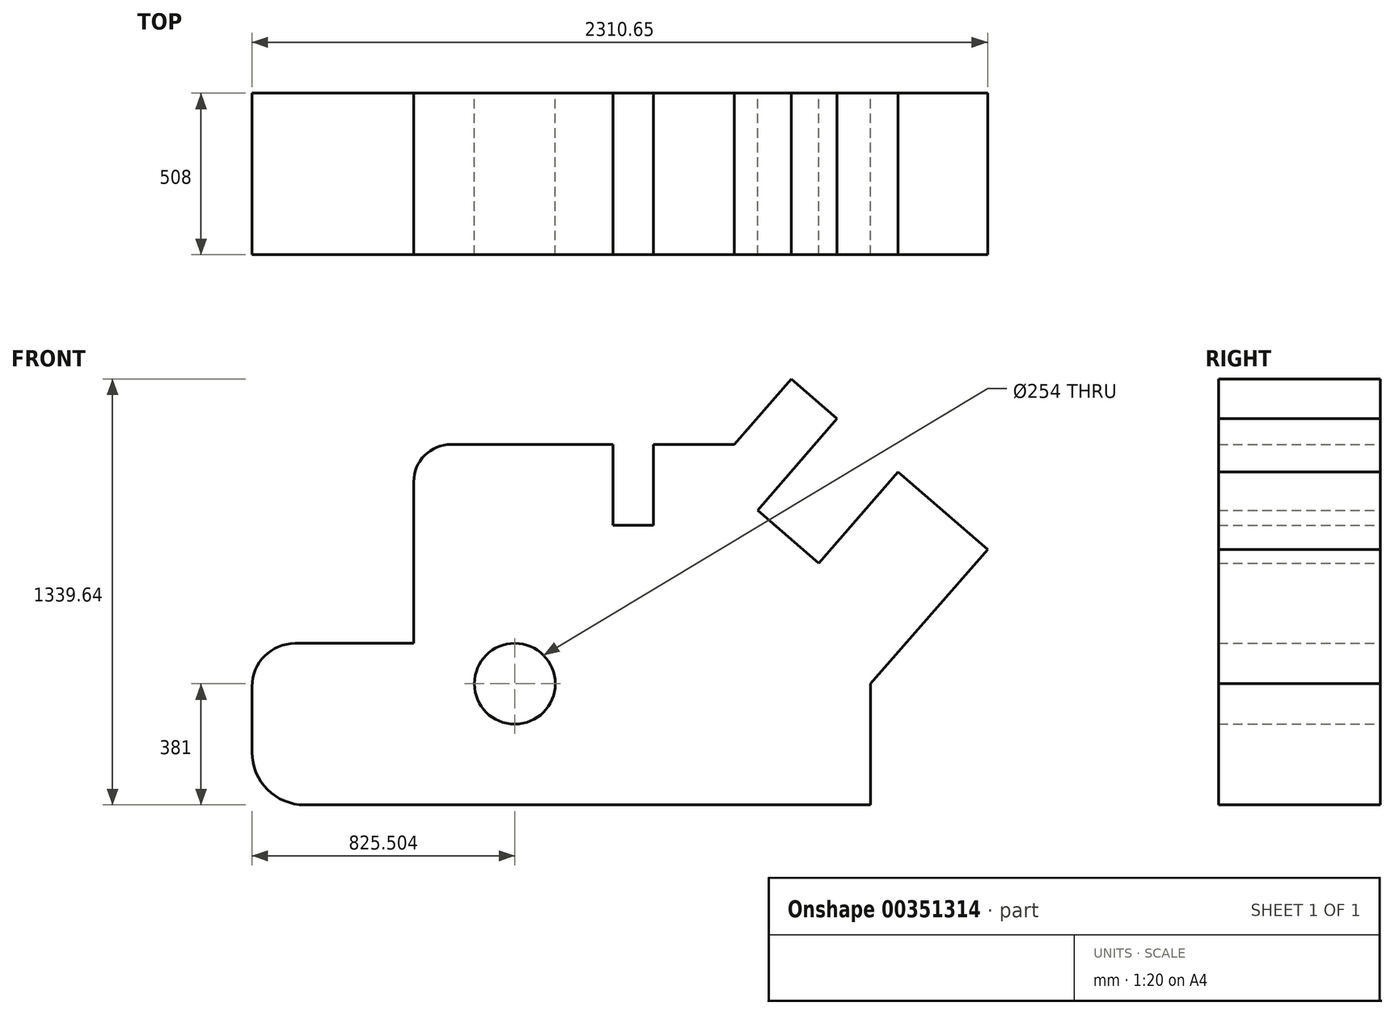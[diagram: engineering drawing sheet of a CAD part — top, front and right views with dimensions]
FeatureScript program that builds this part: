
annotation { "Feature Type Name" : "Feature", "Feature Type Description" : "" }
export const myFeature = defineFeature(function(context is Context, id is Id, definition is map)
    precondition{}
    {
        {
            var Q0;
            Q0=qCreatedBy(makeId("Front.planeOp"),FACE);
            var sketch = newSketch(context, id + "F0", { "sketchPlane" : qUnion([Q0])});
            skLineSegment(sketch, "E0", {"start": v(-36.33, -135.55) * mm, "end": v(-36.33, -342.46) * mm});
            skLineSegment(sketch, "E1", {"start": v(129.21, -508) * mm, "end": v(1907.21, -508) * mm});
            skLineSegment(sketch, "E2", {"start": v(1907.21, -508) * mm, "end": v(1907.21, -127) * mm});
            skLineSegment(sketch, "E3", {"start": v(1907.21, -127) * mm, "end": v(2274.32, 295.55) * mm});
            skLineSegment(sketch, "E4", {"start": v(2274.32, 295.55) * mm, "end": v(1993.46, 539.56) * mm});
            skLineSegment(sketch, "E5", {"start": v(1993.46, 539.56) * mm, "end": v(1743.58, 251.95) * mm});
            skLineSegment(sketch, "E6", {"start": v(1743.58, 251.95) * mm, "end": v(1551.84, 418.54) * mm});
            skLineSegment(sketch, "E7", {"start": v(1551.84, 418.54) * mm, "end": v(1801.71, 706.15) * mm});
            skLineSegment(sketch, "E8", {"start": v(1801.71, 706.15) * mm, "end": v(1657.28, 831.64) * mm});
            skLineSegment(sketch, "E9", {"start": v(1657.28, 831.64) * mm, "end": v(1478.25, 625.58) * mm});
            skLineSegment(sketch, "E10", {"start": v(1478.25, 625.58) * mm, "end": v(1224.25, 625.58) * mm});
            skLineSegment(sketch, "E11", {"start": v(1224.25, 625.58) * mm, "end": v(1224.25, 371.58) * mm});
            skLineSegment(sketch, "E12", {"start": v(1224.25, 371.58) * mm, "end": v(1097.25, 371.58) * mm});
            skLineSegment(sketch, "E13", {"start": v(1097.25, 371.58) * mm, "end": v(1097.25, 625.58) * mm});
            skLineSegment(sketch, "E14", {"start": v(1097.25, 625.58) * mm, "end": v(589.25, 625.58) * mm});
            skLineSegment(sketch, "E15", {"start": v(471.67, 508) * mm, "end": v(471.67, 0) * mm});
            skLineSegment(sketch, "E16", {"start": v(471.67, 0) * mm, "end": v(99.22, 0) * mm});
            skArc(sketch, "E17", {"start": v(589.25, 625.58) * mm, "mid": v(506.11, 591.14) * mm, "end": v(471.67, 508) * mm});
            skArc(sketch, "E18", {"start": v(99.22, 0) * mm, "mid": v(3.38, -39.7) * mm, "end": v(-36.33, -135.55) * mm});
            skPoint(sketch, "E19.orphan", {"position": v(-36.33, 0) * mm});
            skArc(sketch, "E20", {"start": v(-36.33, -342.46) * mm, "mid": v(12.16, -459.52) * mm, "end": v(129.21, -508) * mm});
            skCircle(sketch, "E21", {"center": v(789.17, -127) * mm, "radius": 127 * mm});
            skSolve(sketch);
        }
        {
            var Q0;
            Q0 = qSketchRegion(id + "F0", true);
            extrude(context, id + "F1", {"entities" : qUnion([Q0]), "depth" : 508 * mm});
        }
    });
